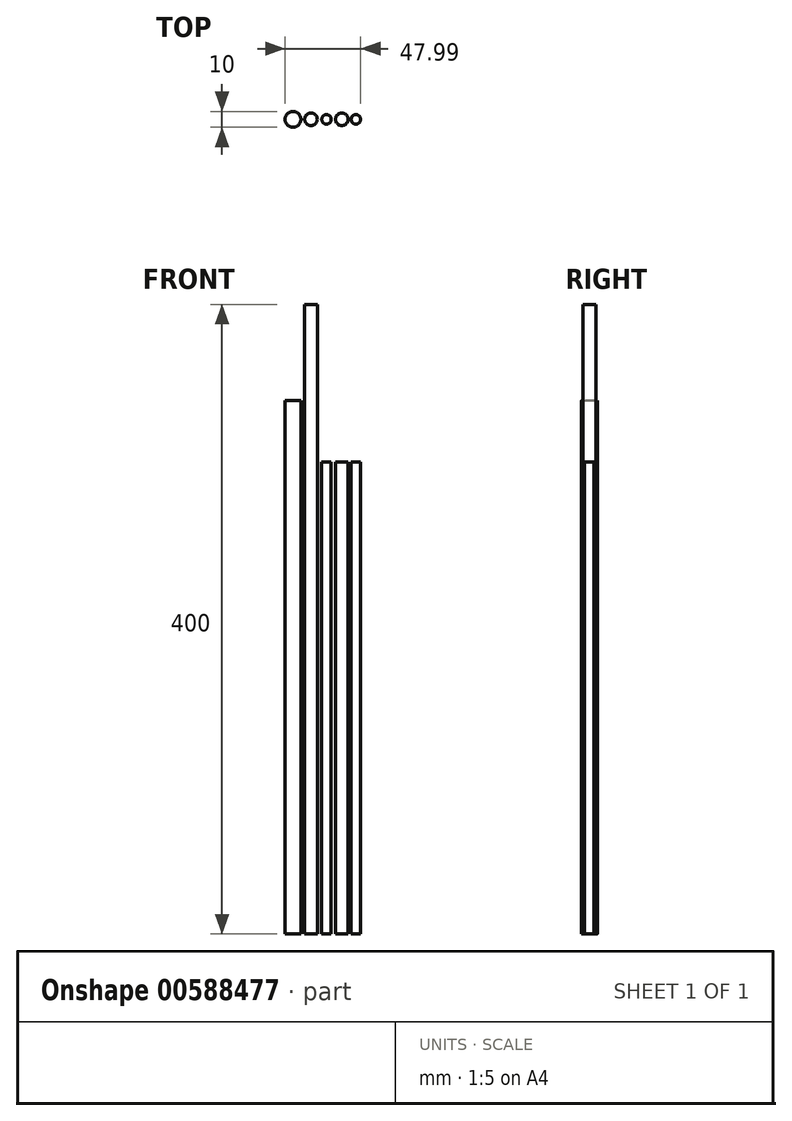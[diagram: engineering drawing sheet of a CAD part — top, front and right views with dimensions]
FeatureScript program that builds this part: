
annotation { "Feature Type Name" : "Feature", "Feature Type Description" : "" }
export const myFeature = defineFeature(function(context is Context, id is Id, definition is map)
    precondition{}
    {
        {
            var Q0;
            Q0=qCreatedBy(makeId("Top.planeOp"),FACE);
            var sketch = newSketch(context, id + "F0", { "sketchPlane" : qUnion([Q0])});
            skLineSegment(sketch, "E0", {"start": v(0, 0) * mm, "end": v(40.66, 0) * mm, "construction": true});
            skCircle(sketch, "E1", {"center": v(0, 0) * mm, "radius": 5 * mm});
            skCircle(sketch, "E2", {"center": v(31.01, 0) * mm, "radius": 4 * mm});
            skCircle(sketch, "E3", {"center": v(39.99, 0) * mm, "radius": 3 * mm});
            skCircle(sketch, "E4", {"center": v(21.27, 0) * mm, "radius": 3 * mm});
            skCircle(sketch, "E5", {"center": v(11.45, 0) * mm, "radius": 4 * mm});
            skSolve(sketch);
        }
        {
            var Q0;
            Q0=makeQuery(id+"F0.imprint","IMPRINT",FACE,{"disambiguationData":[TD([[makeQuery(id+"F0.imprint","IMPRINT",EDGE,{"derivedFrom":sQuery(id+"F0.wireOp",EDGE,"E1")}),1.0]])]});
            extrude(context, id + "F1", {"entities" : qUnion([Q0]), "depth" : 339 * mm, "offsetDistance" : 25 * mm});
        }
        {
            var Q0;
            Q0=makeQuery(id+"F0.imprint","IMPRINT",FACE,{"disambiguationData":[TD([[makeQuery(id+"F0.imprint","IMPRINT",EDGE,{"derivedFrom":sQuery(id+"F0.wireOp",EDGE,"E2")}),1.0]])]});
            extrude(context, id + "F2", {"entities" : qUnion([Q0]), "depth" : 300 * mm, "offsetDistance" : 25 * mm});
        }
        {
            var Q0;
            Q0=makeQuery(id+"F0.imprint","IMPRINT",FACE,{"disambiguationData":[TD([[makeQuery(id+"F0.imprint","IMPRINT",EDGE,{"derivedFrom":sQuery(id+"F0.wireOp",EDGE,"E3")}),1.0]])]});
            extrude(context, id + "F3", {"entities" : qUnion([Q0]), "depth" : 300 * mm, "offsetDistance" : 25 * mm});
        }
        {
            var Q0;
            Q0=makeQuery(id+"F0.imprint","IMPRINT",FACE,{"disambiguationData":[TD([[makeQuery(id+"F0.imprint","IMPRINT",EDGE,{"derivedFrom":sQuery(id+"F0.wireOp",EDGE,"E5")}),1.0]])]});
            extrude(context, id + "F4", {"entities" : qUnion([Q0]), "depth" : 400 * mm, "offsetDistance" : 25 * mm});
        }
        {
            var Q0;
            Q0=makeQuery(id+"F0.imprint","IMPRINT",FACE,{"disambiguationData":[TD([[makeQuery(id+"F0.imprint","IMPRINT",EDGE,{"derivedFrom":sQuery(id+"F0.wireOp",EDGE,"E4")}),1.0]])]});
            extrude(context, id + "F5", {"entities" : qUnion([Q0]), "depth" : 300 * mm, "offsetDistance" : 25 * mm});
        }
    });
